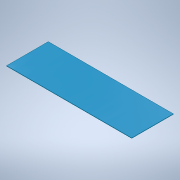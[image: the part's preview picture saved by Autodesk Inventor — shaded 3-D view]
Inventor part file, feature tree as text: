
AUTODESK INVENTOR PART (.ipt)
format: ipt  version: 2020.3 (Build 243373000, 373)  size: 94,208 bytes
history: native  units: mm
features: extrude x1, sketch x1
ambient origin geometry x8: Origin, YZ Plane, XZ Plane, XY Plane, X Axis, Y Axis, Z Axis, Center Point
bodies: Solid1 (feature_tree)
feature tree (2):
  extrude  "Extrusion1"  Depth=156.0mm
  sketch  "Sketch1"  dims[d0=52.0mm d1=156.0mm d2=0.5mm d3=0.0mm]
